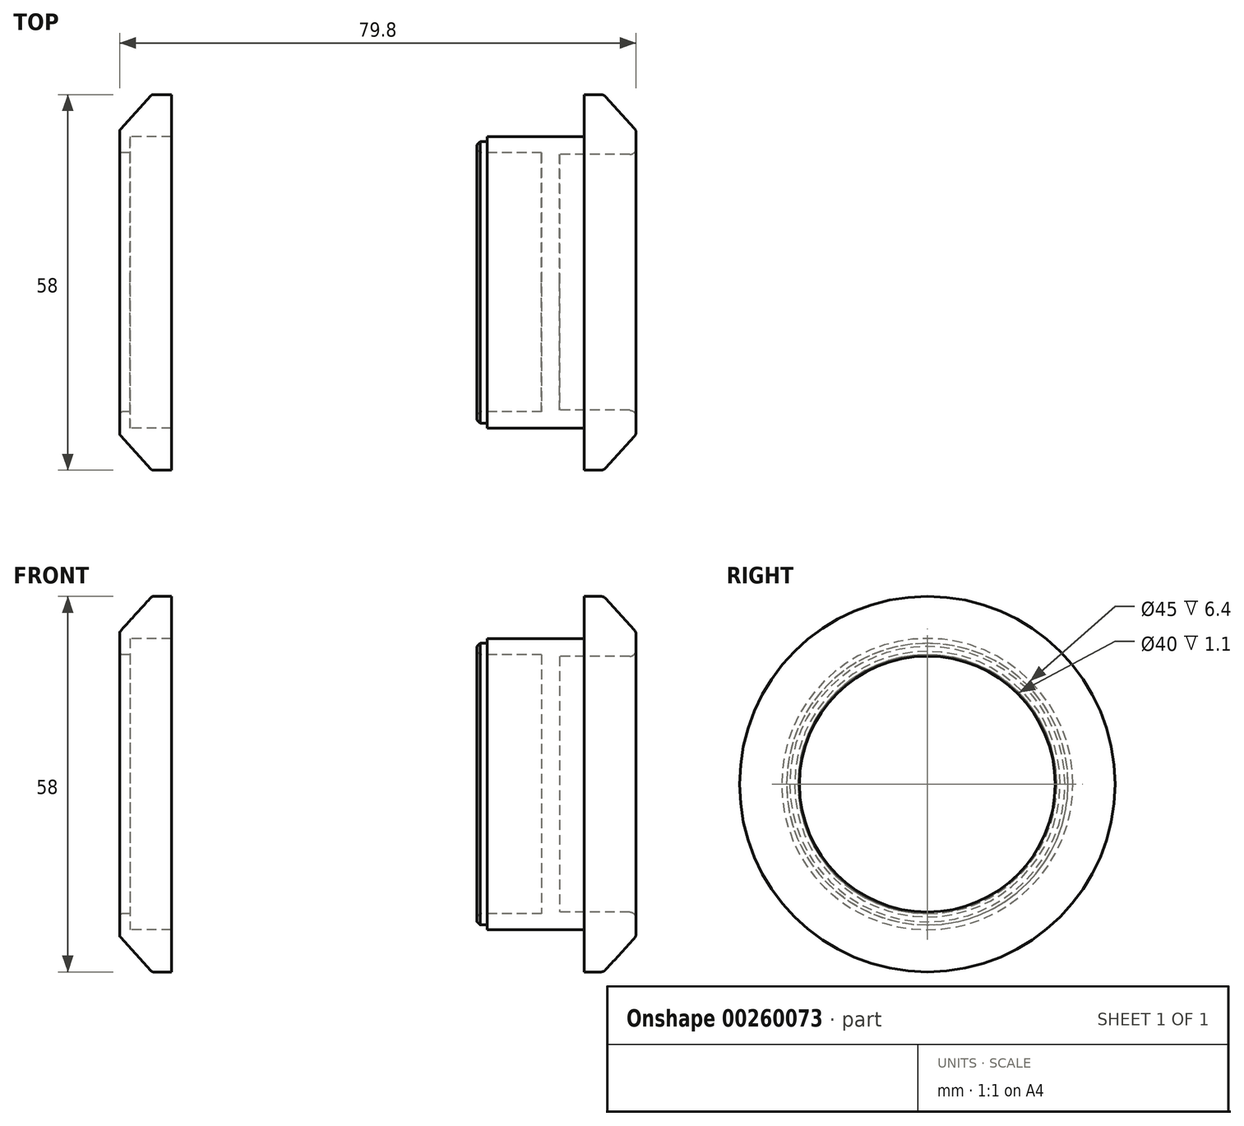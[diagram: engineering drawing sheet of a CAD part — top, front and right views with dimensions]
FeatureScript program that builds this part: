
annotation { "Feature Type Name" : "Feature", "Feature Type Description" : "" }
export const myFeature = defineFeature(function(context is Context, id is Id, definition is map)
    precondition{}
    {
        {
            var Q0;
            Q0=qCreatedBy(makeId("Front.planeOp"),FACE);
            var sketch = newSketch(context, id + "F0", { "sketchPlane" : qUnion([Q0])});
            skLineSegment(sketch, "E0", {"start": v(0, 0) * mm, "end": v(0, 19.75) * mm});
            skLineSegment(sketch, "E1", {"start": v(0, 19.75) * mm, "end": v(11.8, 19.75) * mm});
            skLineSegment(sketch, "E2", {"start": v(11.8, 19.75) * mm, "end": v(11.8, 23.5) * mm});
            skLineSegment(sketch, "E3", {"start": v(11.8, 23.5) * mm, "end": v(6.8, 29) * mm});
            skLineSegment(sketch, "E4", {"start": v(6.8, 29) * mm, "end": v(3.8, 29) * mm});
            skLineSegment(sketch, "E5", {"start": v(3.8, 29) * mm, "end": v(3.8, 22.5) * mm});
            skLineSegment(sketch, "E6", {"start": v(3.8, 22.5) * mm, "end": v(-11.2, 22.5) * mm});
            skLineSegment(sketch, "E7", {"start": v(-12.8, 21.75) * mm, "end": v(-12.8, 20) * mm});
            skLineSegment(sketch, "E8", {"start": v(-12.8, 20) * mm, "end": v(-2.8, 20) * mm});
            skLineSegment(sketch, "E9", {"start": v(-2.8, 20) * mm, "end": v(-2.8, 0) * mm});
            skLineSegment(sketch, "E10", {"start": v(-2.8, 0) * mm, "end": v(0, 0) * mm});
            skLineSegment(sketch, "E11", {"start": v(-11.2, 22.5) * mm, "end": v(-11.2, 21.75) * mm});
            skLineSegment(sketch, "E12", {"start": v(-11.2, 21.75) * mm, "end": v(-12.8, 21.75) * mm});
            skPoint(sketch, "E13.orphan", {"position": v(-12.8, 22.5) * mm});
            skPoint(sketch, "E14.endSnap0", {"position": v(-1.4, 0) * mm});
            skSolve(sketch);
        }
        {
            var Q0;
            Q0=makeQuery(id+"F0.imprint","IMPRINT",FACE,{"disambiguationData":[TD([[makeQuery(id+"F0.imprint","IMPRINT",EDGE,{"derivedFrom":sQuery(id+"F0.wireOp",EDGE,"E0")}),1.0]])]});
            var sketch = newSketch(context, id + "F1", { "sketchPlane" : qUnion([Q0])});
            skLineSegment(sketch, "E15", {"start": v(-14.76, 0) * mm, "end": v(18.36, 0) * mm});
            skSolve(sketch);
        }
        {
            var Q0;
            Q0=makeQuery(id+"F0.imprint","IMPRINT",FACE,{"disambiguationData":[TD([[makeQuery(id+"F0.imprint","IMPRINT",EDGE,{"derivedFrom":sQuery(id+"F0.wireOp",EDGE,"E0")}),1.0]])]});
            var Q1;
            Q1=sQuery(id+"F1.wireOp",EDGE,"E15");
            revolve(context, id + "F2", {"entities" : qUnion([Q0]), "axis" : qUnion([Q1]), "revolveType" : RevolveType.FULL});
        }
        {
            var Q0;
            Q0=makeQuery(id+"F2.opRevolve","SWEPT_EDGE",EDGE,{"disambiguationData":[OSD([sQuery(id+"F0.wireOp",EDGE,"E2"),sQuery(id+"F0.wireOp",EDGE,"E3")])]});
            var Q1;
            Q1=makeQuery(id+"F2.opRevolve","SWEPT_EDGE",EDGE,{"disambiguationData":[OSD([sQuery(id+"F0.wireOp",EDGE,"E1"),sQuery(id+"F0.wireOp",EDGE,"E2")])]});
            var Q2;
            Q2=makeQuery(id+"F2.opRevolve","SWEPT_EDGE",EDGE,{"disambiguationData":[OSD([sQuery(id+"F0.wireOp",EDGE,"E3"),sQuery(id+"F0.wireOp",EDGE,"E4")])]});
            fillet(context, id + "F3", {"entities" : qUnion([Q0, Q1, Q2]), "radius" : 1 * mm, "tangentPropagation" : true, "allowEdgeOverflow" : false});
        }
        {
            var Q0;
            Q0=makeQuery(id+"F2.opRevolve","SWEPT_EDGE",EDGE,{"disambiguationData":[OSD([sQuery(id+"F0.wireOp",EDGE,"E7"),sQuery(id+"F0.wireOp",EDGE,"E12")])]});
            var Q1;
            Q1=makeQuery(id+"F2.opRevolve","SWEPT_EDGE",EDGE,{"disambiguationData":[OSD([sQuery(id+"F0.wireOp",EDGE,"E7"),sQuery(id+"F0.wireOp",EDGE,"E8")])]});
            chamfer(context, id + "F4", {"entities" : qUnion([Q0, Q1]), "width" : .5 * mm, "tangentPropagation" : true});
        }
        {
            var Q0;
            Q0=qCreatedBy(makeId("Front.planeOp"),FACE);
            var sketch = newSketch(context, id + "F5", { "sketchPlane" : qUnion([Q0])});
            skLineSegment(sketch, "E16", {"start": v(-60, 22.5) * mm, "end": v(-60, 29) * mm});
            skLineSegment(sketch, "E17", {"start": v(-60, 29) * mm, "end": v(-63, 29) * mm});
            skLineSegment(sketch, "E18", {"start": v(-63, 29) * mm, "end": v(-68, 23.5) * mm});
            skLineSegment(sketch, "E19", {"start": v(-68, 23.5) * mm, "end": v(-68, 20) * mm});
            skLineSegment(sketch, "E20", {"start": v(-68, 20) * mm, "end": v(-66.4, 20) * mm});
            skLineSegment(sketch, "E21", {"start": v(-66.4, 20) * mm, "end": v(-66.4, 22.5) * mm});
            skLineSegment(sketch, "E22", {"start": v(-66.4, 22.5) * mm, "end": v(-60, 22.5) * mm});
            skPoint(sketch, "E23.orphan", {"position": v(-60, 0) * mm});
            skPoint(sketch, "E24.start.orphan", {"position": v(-68, 0) * mm});
            skSolve(sketch);
        }
        {
            var Q0;
            Q0=makeQuery(id+"F5.imprint","IMPRINT",FACE,{"disambiguationData":[TD([[makeQuery(id+"F5.imprint","IMPRINT",EDGE,{"derivedFrom":sQuery(id+"F5.wireOp",EDGE,"E16")}),1.0]])]});
            var Q1;
            Q1=sQuery(id+"F1.wireOp",EDGE,"E15");
            revolve(context, id + "F6", {"entities" : qUnion([Q0]), "axis" : qUnion([Q1]), "revolveType" : RevolveType.FULL});
        }
        {
            var Q0;
            Q0=makeQuery(id+"F6.opRevolve","SWEPT_EDGE",EDGE,{"disambiguationData":[OSD([sQuery(id+"F5.wireOp",EDGE,"E18"),sQuery(id+"F5.wireOp",EDGE,"E19")])]});
            var Q1;
            Q1=makeQuery(id+"F6.opRevolve","SWEPT_EDGE",EDGE,{"disambiguationData":[OSD([sQuery(id+"F5.wireOp",EDGE,"E17"),sQuery(id+"F5.wireOp",EDGE,"E18")])]});
            var Q2;
            Q2=makeQuery(id+"F6.opRevolve","SWEPT_EDGE",EDGE,{"disambiguationData":[OSD([sQuery(id+"F5.wireOp",EDGE,"E19"),sQuery(id+"F5.wireOp",EDGE,"E20")])]});
            fillet(context, id + "F7", {"entities" : qUnion([Q0, Q1, Q2]), "radius" : .5 * mm, "tangentPropagation" : true, "allowEdgeOverflow" : false});
        }
    });
